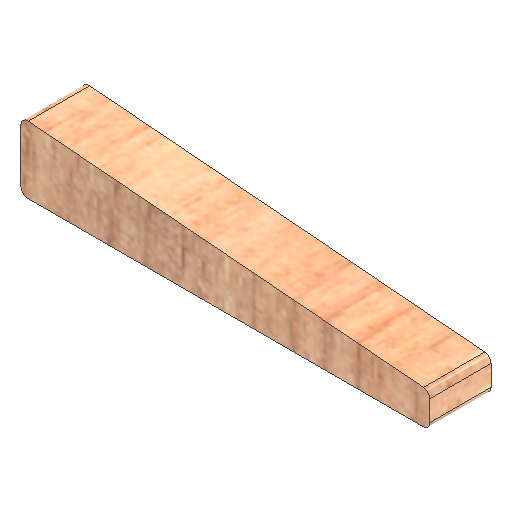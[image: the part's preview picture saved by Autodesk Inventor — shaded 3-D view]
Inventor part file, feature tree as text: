
AUTODESK INVENTOR PART (.ipt)
format: ipt  version: 2021 (Build 250183000, 183)  size: 198,656 bytes
history: native  units: mm
features: other x1, extrude x1
ambient origin geometry x8: Origin, YZ Plane, XZ Plane, XY Plane, X Axis, Y Axis, Z Axis, Center Point
bodies: Solid1 (feature_tree)
feature tree (2):
  other  "CONTOURS"
  extrude  "Extrusion1"  Depth=18.0mm TaperAngle=0.0deg
